# Revit family: ALEX
name_source: partatom
category: Furniture
units: mm (PartAtom-declared; Revit-internal decimal feet)

## family parameters
Always vertical = Yes
Cut with Voids When Loaded = No
OmniClass Number = 23.40.20.00
OmniClass Title = General Furniture and Specialties
Room Calculation Point = No
Shared = No
Work Plane-Based = No

## types (1)
- ALEX
    Depth = 600 mm  [stored 1.9685 ft]
    H = 25 mm  [stored 0.082021 ft]
    H1 = 120 mm  [stored 0.393701 ft]
    H2 = 28 mm  [stored 0.0918635 ft]
    HL = 115 mm
    Height = 760 mm  [stored 2.49344 ft]
    L1 = 20 mm  [stored 0.0656168 ft]
    L2 = 58 mm  [stored 0.190289 ft]
    LMDP = 18 mm  [stored 0.0590551 ft]
    Length = 1310 mm  [stored 4.2979 ft]
    W = 100 mm  [stored 0.328084 ft]

note: [stored X ft] marks values corroborated as IEEE doubles in the binary element streams (Revit-internal decimal feet)

## geometry (parser evidence)
native form markers: Sweep x13
no freeform markers — native parametric forms only
